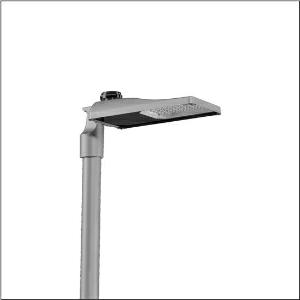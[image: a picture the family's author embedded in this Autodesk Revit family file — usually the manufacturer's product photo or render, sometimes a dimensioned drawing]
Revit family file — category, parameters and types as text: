
# Revit family: streetlight_sl_31_mini___st1_0a_5xh2d3bn08ja_dd0a
name_source: partatom
category: Lighting Fixtures
units: mm (PartAtom-declared; Revit-internal decimal feet)

## family parameters
Cut with Voids When Loaded = No
Host = Face
Light Source = No
Part Type = Normal
Room Calculation Point = No
Round Connector Dimension = Use Diameter
Shared = No

## types (1)
- --- (1 x LED, 12140 lm, 81.1 W, 3000K)
    Apparent Load = 81 VA
    CIE Flux Codes = 40 73 97 100 100
    Color Rendering = 70
    Color Temperature = 3000K
    Default Elevation = 1800 mm
    Description = Streetlight SL 31 mini, mast luminaire, primary light control with lens, of PMMA, primary optical cover: cover, of toughened safety glass, transparent, light distribution: ST1.0a, light emission: direct distribution, primary light characteristic: asymmetric, installation type: post-top, side-entry, LED, High Power LED, rated luminous flux: 12.140lm, luminous efficacy: 150lm/W, light colour: 730, colour temperature: 3000K, control: overheat protection, intelligent temperature release in ECG and LED module, constant luminous flux control, time-dependent luminous flux control, flexible luminous flux parameterisation, presetting dimming linear, with cable H07RN-F 3x 1.5mm², mains connection: 220..240V, AC, 50/60Hz, connection cable pre-assembled, cable length: 10,5m, start of lifetime: 81W, end of service life: 88W, reduction: 36W, luminaire housing, of diecast aluminium, powder-coated, Siteco® metallic grey (DB 702S), corrosivity category C5 high according to DIN EN ISO 12944, no sealing on luminaire upper side, inclination: -15°..+20° (post-top) | -20°..+20° (side-entry), adjustable in 5° steps, mast flange (76/60mm) included as standard, multi-level sealing system, sealing non-destructively replaceable, protection rating (complete): IP66, insulation class (complete): insulation class I (protective earthing), certification: CE, ENEC, ENEC+, VDE, UKCA, impact resistance: IK09, permissible operating ambient temperature for outdoor applications: -40..+50°C, standard-compliant lighting for roads and squares, packaging unit: 1 piece

Light Distribution: ST1.0a
    Height = 76 mm
    Lamp = 1 x LED
    Lamp Light Flux = 12140 lm
    Lamp Power = 81.1 W
    Lamp count = 1
    Length = 547 mm
    Luminous efficacy = 150 lm/W
    Manufacturer = Siteco
    ModVariant = No
    Model = 5XH2D3BN08JA
    Number of Poles = 1
    OnlyDefault = Yes
    Power Factor = 1
    Product Name = Streetlight SL 31 mini | ST1.0a
    Product group = mast luminaire | pylon top
    ProductGroupID = 6100
    Protection Class = Protection class I
    Protection Degree = IP 66
    RLX_Detail_Level = 1
    RLX_Emergency_Light_Flux = 0 lm
    RLX_Emergency_Type = 0
    RLX_Emergency_Type_DB = No
    RlxData = <blob elided: 40553 chars, md5=93f2ac01>
    Socket = socket
    Standby Power = 0 W
    System Light Flux = 12140 lm
    System Power = 81 W
    Type Comments = factory setting: luminous flux: 100 % | dim-lin: 254 | 860 mA
    Type Image = l_1300322.jpg
    URL = http://relux.com
    VarID = @adj_008255
    Voltage = 0 V
    Weight = 0.00 kg
    Width = 265 mm

## geometry (parser evidence)
native form markers: Blend x4, Sweep x10
no freeform markers — native parametric forms only
